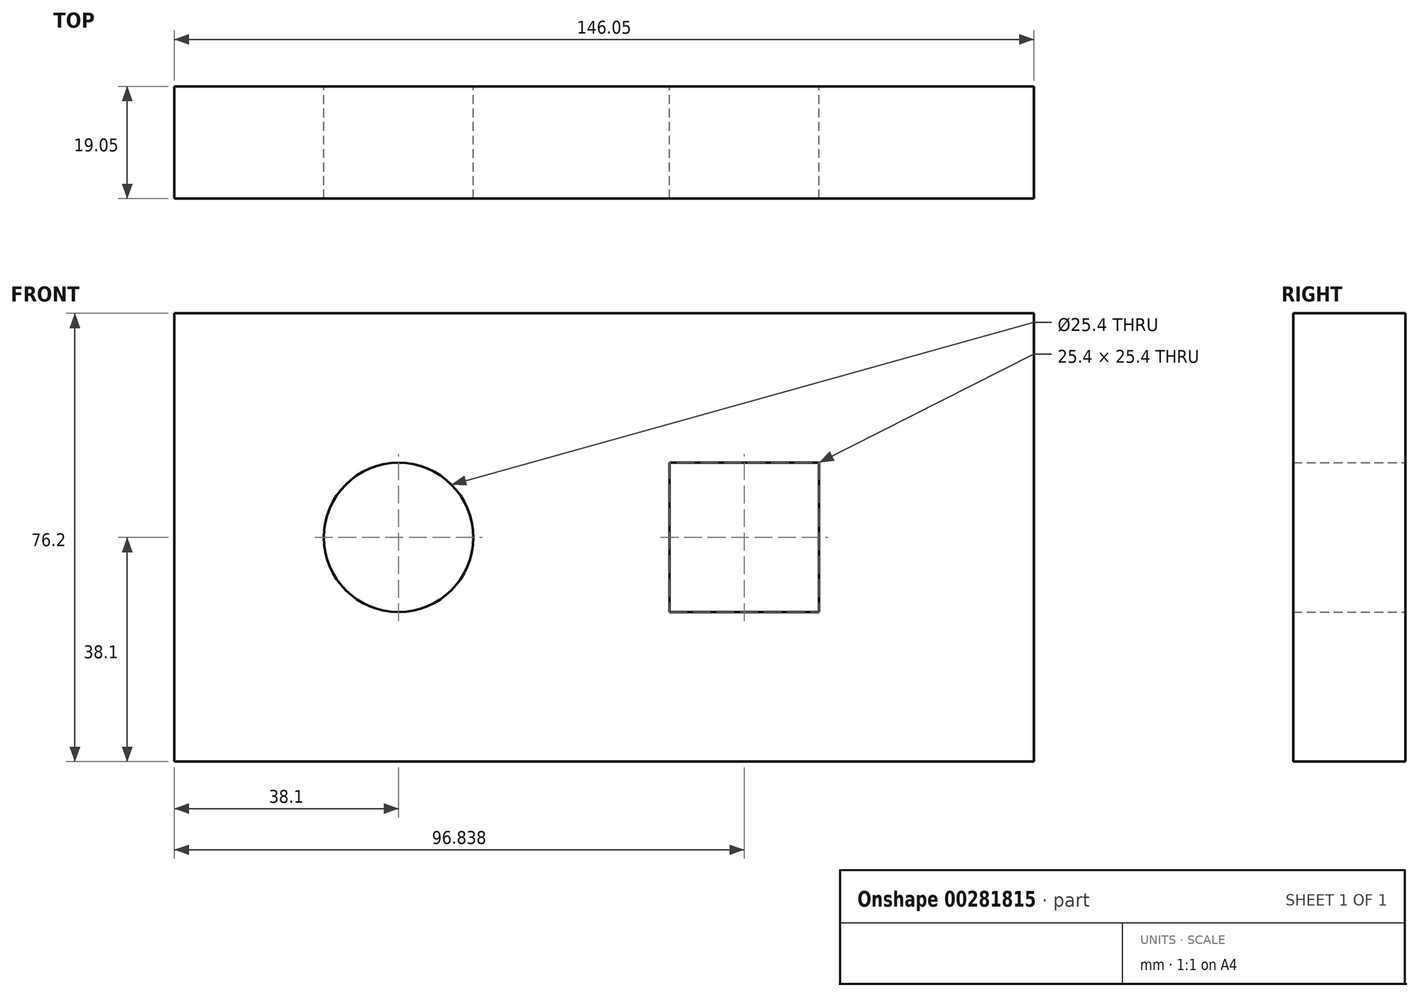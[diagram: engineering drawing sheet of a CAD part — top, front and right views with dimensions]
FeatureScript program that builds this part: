
annotation { "Feature Type Name" : "Feature", "Feature Type Description" : "" }
export const myFeature = defineFeature(function(context is Context, id is Id, definition is map)
    precondition{}
    {
        {
            var Q0;
            Q0=qCreatedBy(makeId("Front.planeOp"),FACE);
            var sketch = newSketch(context, id + "F0", { "sketchPlane" : qUnion([Q0])});
            skLineSegment(sketch, "E0.bottom", {"start": v(0, 0) * mm, "end": v(-146.05, 0) * mm});
            skLineSegment(sketch, "E0.top", {"start": v(0, 76.2) * mm, "end": v(-146.05, 76.2) * mm});
            skLineSegment(sketch, "E0.left", {"start": v(0, 0) * mm, "end": v(0, 76.2) * mm});
            skLineSegment(sketch, "E0.right", {"start": v(-146.05, 0) * mm, "end": v(-146.05, 76.2) * mm});
            skLineSegment(sketch, "E1.bottom", {"start": v(-61.91, 50.8) * mm, "end": v(-36.51, 50.8) * mm});
            skLineSegment(sketch, "E1.top", {"start": v(-61.91, 25.4) * mm, "end": v(-36.51, 25.4) * mm});
            skLineSegment(sketch, "E1.left", {"start": v(-61.91, 50.8) * mm, "end": v(-61.91, 25.4) * mm});
            skLineSegment(sketch, "E1.right", {"start": v(-36.51, 50.8) * mm, "end": v(-36.51, 25.4) * mm});
            skCircle(sketch, "E2", {"center": v(-107.95, 38.1) * mm, "radius": 12.7 * mm});
            skSolve(sketch);
        }
        {
            var Q0;
            Q0 = qSketchRegion(id + "F0", true);
            extrude(context, id + "F1", {"entities" : qUnion([Q0]), "depth" : 19.05 * mm});
        }
    });
